annotation { "Feature Type Name" : "Feature", "Feature Type Description" : "" }
export const myFeature = defineFeature(function(context is Context, id is Id, definition is map)
    precondition{}
    {
        {
            var Q0;
            Q0=qCreatedBy(makeId("Front.planeOp"),FACE);
            var sketch = newSketch(context, id + "F0", { "sketchPlane" : qUnion([Q0])});
            skLineSegment(sketch, "E0", {"start": v(0, 0) * mm, "end": v(42.86, 0) * mm});
            skLineSegment(sketch, "E1", {"start": v(42.86, 0) * mm, "end": v(42.86, 3.17) * mm});
            skLineSegment(sketch, "E2", {"start": v(42.86, 3.17) * mm, "end": v(45.24, 3.17) * mm});
            skLineSegment(sketch, "E3", {"start": v(45.24, 3.17) * mm, "end": v(45.24, 0) * mm});
            skLineSegment(sketch, "E4", {"start": v(45.24, 0) * mm, "end": v(153.99, 0) * mm});
            skLineSegment(sketch, "E5", {"start": v(153.99, 0) * mm, "end": v(153.99, 3.17) * mm});
            skLineSegment(sketch, "E6", {"start": v(153.99, 3.17) * mm, "end": v(156.37, 3.17) * mm});
            skLineSegment(sketch, "E7", {"start": v(156.37, 3.17) * mm, "end": v(156.37, 0) * mm});
            skLineSegment(sketch, "E8", {"start": v(156.37, 0) * mm, "end": v(177.8, 0) * mm});
            skLineSegment(sketch, "E9.0", {"start": v(162.72, 5.08) * mm, "end": v(177.8, 5.08) * mm});
            skLineSegment(sketch, "E9.1", {"start": v(161.45, 6.98) * mm, "end": v(161.45, 6.35) * mm});
            skLineSegment(sketch, "E9.2", {"start": v(150.18, 8.25) * mm, "end": v(160.18, 8.25) * mm});
            skLineSegment(sketch, "E9.3", {"start": v(148.9, 6.35) * mm, "end": v(148.9, 6.98) * mm});
            skLineSegment(sketch, "E9.4", {"start": v(51.6, 5.08) * mm, "end": v(147.64, 5.08) * mm});
            skLineSegment(sketch, "E9.5", {"start": v(0, 5.08) * mm, "end": v(36.51, 5.08) * mm});
            skLineSegment(sketch, "E9.6", {"start": v(37.78, 6.35) * mm, "end": v(37.78, 6.98) * mm});
            skLineSegment(sketch, "E9.7", {"start": v(39.05, 8.25) * mm, "end": v(49.05, 8.25) * mm});
            skLineSegment(sketch, "E9.8", {"start": v(50.32, 6.98) * mm, "end": v(50.32, 6.35) * mm});
            skLineSegment(sketch, "E10", {"start": v(0, 0) * mm, "end": v(0, 5.08) * mm});
            skLineSegment(sketch, "E11", {"start": v(177.8, 0) * mm, "end": v(177.8, 5.08) * mm});
            skPoint(sketch, "E12.visualSharp", {"position": v(161.45, 5.08) * mm});
            skArc(sketch, "E12.filletArc", {"start": v(161.45, 6.35) * mm, "mid": v(161.82, 5.45) * mm, "end": v(162.72, 5.08) * mm});
            skPoint(sketch, "E13.visualSharp", {"position": v(161.45, 8.25) * mm});
            skArc(sketch, "E13.filletArc", {"start": v(161.45, 6.98) * mm, "mid": v(161.08, 7.88) * mm, "end": v(160.18, 8.25) * mm});
            skPoint(sketch, "E14.visualSharp", {"position": v(148.9, 8.25) * mm});
            skArc(sketch, "E14.filletArc", {"start": v(150.18, 8.25) * mm, "mid": v(149.28, 7.88) * mm, "end": v(148.9, 6.98) * mm});
            skPoint(sketch, "E15.visualSharp", {"position": v(148.9, 5.08) * mm});
            skArc(sketch, "E15.filletArc", {"start": v(147.64, 5.08) * mm, "mid": v(148.54, 5.45) * mm, "end": v(148.9, 6.35) * mm});
            skPoint(sketch, "E16.visualSharp", {"position": v(50.32, 5.08) * mm});
            skArc(sketch, "E16.filletArc", {"start": v(50.32, 6.35) * mm, "mid": v(50.7, 5.45) * mm, "end": v(51.6, 5.08) * mm});
            skPoint(sketch, "E17.visualSharp", {"position": v(50.32, 8.25) * mm});
            skArc(sketch, "E17.filletArc", {"start": v(50.32, 6.98) * mm, "mid": v(49.95, 7.88) * mm, "end": v(49.05, 8.25) * mm});
            skPoint(sketch, "E18.visualSharp", {"position": v(37.78, 8.25) * mm});
            skArc(sketch, "E18.filletArc", {"start": v(39.05, 8.25) * mm, "mid": v(38.15, 7.88) * mm, "end": v(37.78, 6.98) * mm});
            skPoint(sketch, "E19.visualSharp", {"position": v(37.78, 5.08) * mm});
            skArc(sketch, "E19.filletArc", {"start": v(36.51, 5.08) * mm, "mid": v(37.41, 5.45) * mm, "end": v(37.78, 6.35) * mm});
            skSolve(sketch);
        }
        {
            var Q0;
            Q0 = qSketchRegion(id + "F0", true);
            extrude(context, id + "F1", {"entities" : qUnion([Q0]), "endBound" : BoundingType.SYMMETRIC, "depth" : 44.45 * mm, "offsetDistance" : 25.4 * mm});
        }
        {
            var Q0;
            Q0=qCreatedBy(makeId("Top.planeOp"),FACE);
            var sketch = newSketch(context, id + "F2", { "sketchPlane" : qUnion([Q0])});
            skLineSegment(sketch, "E20", {"start": v(-14.1, 0) * mm, "end": v(126.69, 0) * mm, "construction": true});
            skLineSegment(sketch, "E21.bottom", {"start": v(27.6, 17.15) * mm, "end": v(29.65, 17.15) * mm});
            skLineSegment(sketch, "E21.top", {"start": v(16.56, 2.54) * mm, "end": v(29.65, 2.54) * mm});
            skLineSegment(sketch, "E21.left", {"start": v(5.08, 15.37) * mm, "end": v(5.08, 6.83) * mm});
            skLineSegment(sketch, "E21.right", {"start": v(31.43, 15.37) * mm, "end": v(31.43, 4.32) * mm});
            skLineSegment(sketch, "E22.bottom", {"start": v(64.83, 17.14) * mm, "end": v(66.99, 17.14) * mm});
            skLineSegment(sketch, "E22.top", {"start": v(68.15, 2.54) * mm, "end": v(70.3, 2.54) * mm});
            skLineSegment(sketch, "E22.left", {"start": v(56.67, 8.99) * mm, "end": v(56.67, 6.83) * mm});
            skLineSegment(sketch, "E23", {"start": v(8.12, 5.58) * mm, "end": v(16.65, 14.1) * mm});
            skLineSegment(sketch, "E24", {"start": v(15.3, 5.58) * mm, "end": v(26.35, 16.62) * mm});
            skArc(sketch, "E25.filletArc", {"start": v(27.6, 17.15) * mm, "mid": v(26.93, 17) * mm, "end": v(26.35, 16.62) * mm});
            skPoint(sketch, "E26.visualSharp", {"position": v(31.43, 17.14) * mm});
            skArc(sketch, "E26.filletArc", {"start": v(31.43, 15.37) * mm, "mid": v(30.91, 16.62) * mm, "end": v(29.65, 17.15) * mm});
            skPoint(sketch, "E27.visualSharp", {"position": v(31.43, 2.54) * mm});
            skArc(sketch, "E27.filletArc", {"start": v(29.65, 2.54) * mm, "mid": v(30.91, 3.06) * mm, "end": v(31.43, 4.32) * mm});
            skArc(sketch, "E28.filletArc", {"start": v(15.3, 5.58) * mm, "mid": v(14.91, 3.64) * mm, "end": v(16.56, 2.54) * mm});
            skPoint(sketch, "E29.visualSharp", {"position": v(5.08, 2.54) * mm});
            skArc(sketch, "E29.filletArc", {"start": v(5.08, 6.83) * mm, "mid": v(6.18, 5.19) * mm, "end": v(8.12, 5.58) * mm});
            skLineSegment(sketch, "E30", {"start": v(15.4, 17.14) * mm, "end": v(6.86, 17.14) * mm});
            skPoint(sketch, "E31.visualSharp", {"position": v(19.69, 17.14) * mm});
            skArc(sketch, "E31.filletArc", {"start": v(16.65, 14.1) * mm, "mid": v(17.04, 16.05) * mm, "end": v(15.4, 17.15) * mm});
            skPoint(sketch, "E32.visualSharp", {"position": v(5.08, 17.14) * mm});
            skArc(sketch, "E32.filletArc", {"start": v(6.86, 17.14) * mm, "mid": v(5.6, 16.62) * mm, "end": v(5.08, 15.37) * mm});
            skLineSegment(sketch, "E33", {"start": v(59.7, 5.58) * mm, "end": v(68.24, 14.1) * mm});
            skLineSegment(sketch, "E34", {"start": v(66.9, 5.58) * mm, "end": v(77.94, 16.62) * mm});
            skLineSegment(sketch, "E35", {"start": v(71.56, 3.06) * mm, "end": v(82.61, 14.1) * mm});
            skLineSegment(sketch, "E36", {"start": v(81.26, 5.58) * mm, "end": v(92.31, 16.62) * mm});
            skLineSegment(sketch, "E37", {"start": v(85.93, 3.06) * mm, "end": v(96.98, 14.1) * mm});
            skLineSegment(sketch, "E38", {"start": v(95.63, 5.58) * mm, "end": v(106.68, 16.62) * mm});
            skLineSegment(sketch, "E39", {"start": v(100.3, 3.06) * mm, "end": v(111.35, 14.1) * mm});
            skLineSegment(sketch, "E40", {"start": v(110, 5.58) * mm, "end": v(121.05, 16.62) * mm});
            skLineSegment(sketch, "E41", {"start": v(114.67, 3.06) * mm, "end": v(125.72, 14.1) * mm});
            skLineSegment(sketch, "E42", {"start": v(124.37, 5.58) * mm, "end": v(135.42, 16.62) * mm});
            skLineSegment(sketch, "E43", {"start": v(129.04, 3.06) * mm, "end": v(140.09, 14.1) * mm});
            skLineSegment(sketch, "E44", {"start": v(136.6, 3.45) * mm, "end": v(141.65, 8.49) * mm});
            skLineSegment(sketch, "E45.trimOffspring", {"start": v(79.2, 17.15) * mm, "end": v(81.35, 17.15) * mm});
            skLineSegment(sketch, "E46.trimOffspring", {"start": v(82.52, 2.54) * mm, "end": v(84.67, 2.54) * mm});
            skLineSegment(sketch, "E47.trimOffspring", {"start": v(93.57, 17.15) * mm, "end": v(95.72, 17.15) * mm});
            skLineSegment(sketch, "E48.trimOffspring", {"start": v(107.94, 17.15) * mm, "end": v(110.1, 17.15) * mm});
            skLineSegment(sketch, "E49.trimOffspring", {"start": v(96.89, 2.54) * mm, "end": v(99.04, 2.54) * mm});
            skLineSegment(sketch, "E50.trimOffspring", {"start": v(122.3, 17.15) * mm, "end": v(124.46, 17.15) * mm});
            skLineSegment(sketch, "E51.trimOffspring", {"start": v(111.26, 2.54) * mm, "end": v(113.41, 2.54) * mm});
            skLineSegment(sketch, "E52.trimOffspring", {"start": v(136.67, 17.15) * mm, "end": v(138.83, 17.15) * mm});
            skLineSegment(sketch, "E53.trimOffspring", {"start": v(125.62, 2.54) * mm, "end": v(127.78, 2.54) * mm});
            skLineSegment(sketch, "E54.trimOffspring", {"start": v(136.98, 2.54) * mm, "end": v(140.78, 2.54) * mm});
            skLineSegment(sketch, "E55.trimOffspring", {"start": v(142.56, 8.11) * mm, "end": v(142.56, 4.32) * mm});
            skPoint(sketch, "E56.visualSharp", {"position": v(71.28, 17.14) * mm});
            skArc(sketch, "E56.filletArc", {"start": v(68.24, 14.1) * mm, "mid": v(68.63, 16.05) * mm, "end": v(66.99, 17.14) * mm});
            skPoint(sketch, "E57.visualSharp", {"position": v(56.67, 2.54) * mm});
            skArc(sketch, "E57.filletArc", {"start": v(56.67, 6.83) * mm, "mid": v(57.77, 5.19) * mm, "end": v(59.7, 5.58) * mm});
            skPoint(sketch, "E58.visualSharp", {"position": v(56.67, 17.14) * mm});
            skPoint(sketch, "E59.visualSharp", {"position": v(63.86, 2.54) * mm});
            skArc(sketch, "E59.filletArc", {"start": v(66.9, 5.58) * mm, "mid": v(66.5, 3.64) * mm, "end": v(68.15, 2.54) * mm});
            skPoint(sketch, "E60.visualSharp", {"position": v(71.04, 2.54) * mm});
            skArc(sketch, "E60.filletArc", {"start": v(70.3, 2.54) * mm, "mid": v(70.99, 2.68) * mm, "end": v(71.56, 3.06) * mm});
            skPoint(sketch, "E61.visualSharp", {"position": v(85.65, 17.14) * mm});
            skArc(sketch, "E61.filletArc", {"start": v(82.61, 14.1) * mm, "mid": v(83, 16.05) * mm, "end": v(81.35, 17.14) * mm});
            skPoint(sketch, "E62.visualSharp", {"position": v(78.46, 17.14) * mm});
            skArc(sketch, "E62.filletArc", {"start": v(79.2, 17.15) * mm, "mid": v(78.52, 17) * mm, "end": v(77.94, 16.62) * mm});
            skPoint(sketch, "E63.visualSharp", {"position": v(92.83, 17.14) * mm});
            skArc(sketch, "E63.filletArc", {"start": v(93.57, 17.14) * mm, "mid": v(92.89, 17) * mm, "end": v(92.31, 16.62) * mm});
            skPoint(sketch, "E64.visualSharp", {"position": v(100.02, 17.14) * mm});
            skArc(sketch, "E64.filletArc", {"start": v(96.98, 14.1) * mm, "mid": v(97.37, 16.05) * mm, "end": v(95.72, 17.15) * mm});
            skPoint(sketch, "E65.visualSharp", {"position": v(85.41, 2.54) * mm});
            skArc(sketch, "E65.filletArc", {"start": v(84.67, 2.54) * mm, "mid": v(85.35, 2.68) * mm, "end": v(85.93, 3.06) * mm});
            skPoint(sketch, "E66.visualSharp", {"position": v(78.23, 2.54) * mm});
            skArc(sketch, "E66.filletArc", {"start": v(81.26, 5.58) * mm, "mid": v(80.88, 3.64) * mm, "end": v(82.52, 2.54) * mm});
            skPoint(sketch, "E67.visualSharp", {"position": v(107.2, 17.14) * mm});
            skArc(sketch, "E67.filletArc", {"start": v(107.94, 17.15) * mm, "mid": v(107.26, 17) * mm, "end": v(106.68, 16.62) * mm});
            skPoint(sketch, "E68.visualSharp", {"position": v(114.38, 17.14) * mm});
            skArc(sketch, "E68.filletArc", {"start": v(111.35, 14.1) * mm, "mid": v(111.73, 16.05) * mm, "end": v(110.1, 17.15) * mm});
            skPoint(sketch, "E69.visualSharp", {"position": v(99.78, 2.54) * mm});
            skArc(sketch, "E69.filletArc", {"start": v(99.04, 2.54) * mm, "mid": v(99.72, 2.68) * mm, "end": v(100.3, 3.06) * mm});
            skPoint(sketch, "E70.visualSharp", {"position": v(92.6, 2.54) * mm});
            skArc(sketch, "E70.filletArc", {"start": v(95.63, 5.58) * mm, "mid": v(95.24, 3.64) * mm, "end": v(96.89, 2.54) * mm});
            skPoint(sketch, "E71.visualSharp", {"position": v(106.96, 2.54) * mm});
            skArc(sketch, "E71.filletArc", {"start": v(110, 5.58) * mm, "mid": v(109.61, 3.64) * mm, "end": v(111.26, 2.54) * mm});
            skPoint(sketch, "E72.visualSharp", {"position": v(114.15, 2.54) * mm});
            skArc(sketch, "E72.filletArc", {"start": v(113.41, 2.54) * mm, "mid": v(114.1, 2.68) * mm, "end": v(114.67, 3.06) * mm});
            skPoint(sketch, "E73.visualSharp", {"position": v(128.75, 17.14) * mm});
            skArc(sketch, "E73.filletArc", {"start": v(125.72, 14.1) * mm, "mid": v(126.1, 16.05) * mm, "end": v(124.46, 17.15) * mm});
            skPoint(sketch, "E74.visualSharp", {"position": v(121.57, 17.14) * mm});
            skArc(sketch, "E74.filletArc", {"start": v(122.3, 17.15) * mm, "mid": v(121.62, 17) * mm, "end": v(121.05, 16.62) * mm});
            skPoint(sketch, "E75.visualSharp", {"position": v(135.94, 17.14) * mm});
            skArc(sketch, "E75.filletArc", {"start": v(136.67, 17.14) * mm, "mid": v(136, 17) * mm, "end": v(135.42, 16.62) * mm});
            skPoint(sketch, "E76.visualSharp", {"position": v(128.52, 2.54) * mm});
            skArc(sketch, "E76.filletArc", {"start": v(127.78, 2.54) * mm, "mid": v(128.46, 2.68) * mm, "end": v(129.04, 3.06) * mm});
            skPoint(sketch, "E77.visualSharp", {"position": v(121.33, 2.54) * mm});
            skArc(sketch, "E77.filletArc", {"start": v(124.37, 5.58) * mm, "mid": v(123.98, 3.64) * mm, "end": v(125.62, 2.54) * mm});
            skPoint(sketch, "E78.visualSharp", {"position": v(142.56, 2.54) * mm});
            skArc(sketch, "E78.filletArc", {"start": v(140.78, 2.54) * mm, "mid": v(142.04, 3.06) * mm, "end": v(142.56, 4.32) * mm});
            skPoint(sketch, "E79.visualSharp", {"position": v(135.7, 2.54) * mm});
            skArc(sketch, "E79.filletArc", {"start": v(136.6, 3.45) * mm, "mid": v(136.5, 2.87) * mm, "end": v(136.98, 2.54) * mm});
            skPoint(sketch, "E80.visualSharp", {"position": v(142.56, 9.4) * mm});
            skArc(sketch, "E80.filletArc", {"start": v(142.56, 8.11) * mm, "mid": v(142.23, 8.6) * mm, "end": v(141.65, 8.49) * mm});
            skArc(sketch, "E81.MirrorCS", {"start": v(143.12, -17.14) * mm, "mid": v(142.85, -17.26) * mm, "end": v(142.56, -17.32) * mm});
            skArc(sketch, "E82.MirrorCS", {"start": v(136.6, -3.45) * mm, "mid": v(136.5, -2.87) * mm, "end": v(136.98, -2.54) * mm});
            skArc(sketch, "E83.MirrorCS", {"start": v(107.94, -17.15) * mm, "mid": v(107.26, -17) * mm, "end": v(106.68, -16.62) * mm});
            skArc(sketch, "E84.MirrorCS", {"start": v(93.57, -17.14) * mm, "mid": v(92.89, -17) * mm, "end": v(92.31, -16.62) * mm});
            skArc(sketch, "E85.MirrorCS", {"start": v(99.04, -2.54) * mm, "mid": v(99.72, -2.68) * mm, "end": v(100.3, -3.06) * mm});
            skArc(sketch, "E86.MirrorCS", {"start": v(122.3, -17.15) * mm, "mid": v(121.62, -17) * mm, "end": v(121.05, -16.62) * mm});
            skArc(sketch, "E87.MirrorCS", {"start": v(84.67, -2.54) * mm, "mid": v(85.35, -2.68) * mm, "end": v(85.93, -3.06) * mm});
            skArc(sketch, "E88.MirrorCS", {"start": v(136.67, -17.14) * mm, "mid": v(136, -17) * mm, "end": v(135.42, -16.62) * mm});
            skArc(sketch, "E89.MirrorCS", {"start": v(142.56, -8.11) * mm, "mid": v(142.23, -8.6) * mm, "end": v(141.65, -8.49) * mm});
            skArc(sketch, "E90.MirrorCS", {"start": v(113.41, -2.54) * mm, "mid": v(114.1, -2.68) * mm, "end": v(114.67, -3.06) * mm});
            skLineSegment(sketch, "E91.MirrorCS", {"start": v(142.56, -8.11) * mm, "end": v(142.56, -4.32) * mm});
            skLineSegment(sketch, "E92.MirrorCS", {"start": v(136.98, -2.54) * mm, "end": v(140.78, -2.54) * mm});
            skArc(sketch, "E93.MirrorCS", {"start": v(127.78, -2.54) * mm, "mid": v(128.46, -2.68) * mm, "end": v(129.04, -3.06) * mm});
            skArc(sketch, "E94.MirrorCS", {"start": v(79.2, -17.15) * mm, "mid": v(78.52, -17) * mm, "end": v(77.94, -16.62) * mm});
            skArc(sketch, "E95.MirrorCS", {"start": v(70.3, -2.54) * mm, "mid": v(70.99, -2.68) * mm, "end": v(71.56, -3.06) * mm});
            skLineSegment(sketch, "E96.MirrorCS", {"start": v(142.56, -17.32) * mm, "end": v(142.56, -15.37) * mm});
            skLineSegment(sketch, "E97.MirrorCS", {"start": v(68.15, -2.54) * mm, "end": v(70.3, -2.54) * mm});
            skLineSegment(sketch, "E98.MirrorCS", {"start": v(136.6, -3.45) * mm, "end": v(141.65, -8.49) * mm});
            skLineSegment(sketch, "E99.MirrorCS", {"start": v(111.26, -2.54) * mm, "end": v(113.41, -2.54) * mm});
            skLineSegment(sketch, "E100.MirrorCS", {"start": v(136.67, -17.15) * mm, "end": v(143.32, -17.15) * mm});
            skLineSegment(sketch, "E101.MirrorCS", {"start": v(122.3, -17.15) * mm, "end": v(124.46, -17.15) * mm});
            skLineSegment(sketch, "E102.MirrorCS", {"start": v(79.2, -17.15) * mm, "end": v(81.35, -17.15) * mm});
            skLineSegment(sketch, "E103.MirrorCS", {"start": v(82.52, -2.54) * mm, "end": v(84.67, -2.54) * mm});
            skLineSegment(sketch, "E104.MirrorCS", {"start": v(96.89, -2.54) * mm, "end": v(99.04, -2.54) * mm});
            skLineSegment(sketch, "E105.MirrorCS", {"start": v(93.57, -17.15) * mm, "end": v(95.72, -17.15) * mm});
            skArc(sketch, "E106.MirrorCS", {"start": v(140.78, -2.54) * mm, "mid": v(142.04, -3.06) * mm, "end": v(142.56, -4.32) * mm});
            skLineSegment(sketch, "E107.MirrorCS", {"start": v(107.94, -17.15) * mm, "end": v(110.1, -17.15) * mm});
            skLineSegment(sketch, "E108.MirrorCS", {"start": v(125.62, -2.54) * mm, "end": v(127.78, -2.54) * mm});
            skLineSegment(sketch, "E109.MirrorCS", {"start": v(27.6, -17.15) * mm, "end": v(29.65, -17.15) * mm});
            skArc(sketch, "E110.MirrorCS", {"start": v(27.6, -17.15) * mm, "mid": v(26.93, -17) * mm, "end": v(26.35, -16.62) * mm});
            skArc(sketch, "E111.MirrorCS", {"start": v(6.86, -17.14) * mm, "mid": v(5.6, -16.62) * mm, "end": v(5.08, -15.37) * mm});
            skArc(sketch, "E112.MirrorCS", {"start": v(95.63, -5.58) * mm, "mid": v(95.24, -3.64) * mm, "end": v(96.89, -2.54) * mm});
            skPoint(sketch, "E113.MirrorP", {"position": v(142.56, -2.54) * mm});
            skArc(sketch, "E114.MirrorCS", {"start": v(29.65, -2.54) * mm, "mid": v(30.91, -3.06) * mm, "end": v(31.43, -4.32) * mm});
            skArc(sketch, "E115.MirrorCS", {"start": v(111.35, -14.1) * mm, "mid": v(111.73, -16.05) * mm, "end": v(110.1, -17.15) * mm});
            skArc(sketch, "E116.MirrorCS", {"start": v(124.37, -5.58) * mm, "mid": v(123.98, -3.64) * mm, "end": v(125.62, -2.54) * mm});
            skArc(sketch, "E117.MirrorCS", {"start": v(82.61, -14.1) * mm, "mid": v(83, -16.05) * mm, "end": v(81.35, -17.14) * mm});
            skArc(sketch, "E118.MirrorCS", {"start": v(66.9, -5.58) * mm, "mid": v(66.5, -3.64) * mm, "end": v(68.15, -2.54) * mm});
            skArc(sketch, "E119.MirrorCS", {"start": v(81.26, -5.58) * mm, "mid": v(80.88, -3.64) * mm, "end": v(82.52, -2.54) * mm});
            skLineSegment(sketch, "E120.MirrorCS", {"start": v(15.4, -17.14) * mm, "end": v(6.86, -17.14) * mm});
            skArc(sketch, "E121.MirrorCS", {"start": v(142.56, -15.37) * mm, "mid": v(143.2, -16.14) * mm, "end": v(143.32, -17.15) * mm});
            skPoint(sketch, "E122.MirrorP", {"position": v(142.56, -16.58) * mm});
            skArc(sketch, "E123.MirrorCS", {"start": v(125.72, -14.1) * mm, "mid": v(126.1, -16.05) * mm, "end": v(124.46, -17.15) * mm});
            skArc(sketch, "E124.MirrorCS", {"start": v(96.98, -14.1) * mm, "mid": v(97.37, -16.05) * mm, "end": v(95.72, -17.15) * mm});
            skPoint(sketch, "E125.MirrorP", {"position": v(135.7, -2.54) * mm});
            skArc(sketch, "E126.MirrorCS", {"start": v(16.65, -14.1) * mm, "mid": v(17.04, -16.05) * mm, "end": v(15.4, -17.15) * mm});
            skArc(sketch, "E127.MirrorCS", {"start": v(5.08, -6.83) * mm, "mid": v(6.18, -5.19) * mm, "end": v(8.12, -5.58) * mm});
            skArc(sketch, "E128.MirrorCS", {"start": v(110, -5.58) * mm, "mid": v(109.61, -3.64) * mm, "end": v(111.26, -2.54) * mm});
            skArc(sketch, "E129.MirrorCS", {"start": v(15.3, -5.58) * mm, "mid": v(14.91, -3.64) * mm, "end": v(16.56, -2.54) * mm});
            skArc(sketch, "E130.MirrorCS", {"start": v(31.43, -15.37) * mm, "mid": v(30.91, -16.62) * mm, "end": v(29.65, -17.15) * mm});
            skLineSegment(sketch, "E131.MirrorCS", {"start": v(110, -5.58) * mm, "end": v(121.05, -16.62) * mm});
            skLineSegment(sketch, "E132.MirrorCS", {"start": v(95.63, -5.58) * mm, "end": v(106.68, -16.62) * mm});
            skPoint(sketch, "E133.MirrorP", {"position": v(99.78, -2.54) * mm});
            skLineSegment(sketch, "E134.MirrorCS", {"start": v(71.56, -3.06) * mm, "end": v(82.61, -14.1) * mm});
            skLineSegment(sketch, "E135.MirrorCS", {"start": v(31.43, -15.37) * mm, "end": v(31.43, -4.32) * mm});
            skPoint(sketch, "E136.MirrorP", {"position": v(114.38, -17.14) * mm});
            skPoint(sketch, "E137.MirrorP", {"position": v(19.69, -17.14) * mm});
            skPoint(sketch, "E138.MirrorP", {"position": v(142.56, -17.14) * mm});
            skLineSegment(sketch, "E139.MirrorCS", {"start": v(81.26, -5.58) * mm, "end": v(92.31, -16.62) * mm});
            skPoint(sketch, "E140.MirrorP", {"position": v(31.43, -2.54) * mm});
            skPoint(sketch, "E141.MirrorP", {"position": v(100.02, -17.14) * mm});
            skPoint(sketch, "E142.MirrorP", {"position": v(114.15, -2.54) * mm});
            skPoint(sketch, "E143.MirrorP", {"position": v(5.08, -17.14) * mm});
            skLineSegment(sketch, "E144.MirrorCS", {"start": v(114.67, -3.06) * mm, "end": v(125.72, -14.1) * mm});
            skPoint(sketch, "E145.MirrorP", {"position": v(92.83, -17.14) * mm});
            skPoint(sketch, "E146.MirrorP", {"position": v(106.96, -2.54) * mm});
            skPoint(sketch, "E147.MirrorP", {"position": v(85.41, -2.54) * mm});
            skLineSegment(sketch, "E148.MirrorCS", {"start": v(129.04, -3.06) * mm, "end": v(143.12, -17.14) * mm});
            skLineSegment(sketch, "E149.MirrorCS", {"start": v(66.9, -5.58) * mm, "end": v(77.94, -16.62) * mm});
            skPoint(sketch, "E150.MirrorP", {"position": v(142.56, -9.4) * mm});
            skPoint(sketch, "E151.MirrorP", {"position": v(78.23, -2.54) * mm});
            skPoint(sketch, "E152.MirrorP", {"position": v(121.57, -17.14) * mm});
            skPoint(sketch, "E153.MirrorP", {"position": v(121.33, -2.54) * mm});
            skPoint(sketch, "E154.MirrorP", {"position": v(31.43, -17.14) * mm});
            skPoint(sketch, "E155.MirrorP", {"position": v(92.6, -2.54) * mm});
            skPoint(sketch, "E156.MirrorP", {"position": v(85.65, -17.14) * mm});
            skPoint(sketch, "E157.MirrorP", {"position": v(5.08, -2.54) * mm});
            skLineSegment(sketch, "E158.MirrorCS", {"start": v(100.3, -3.06) * mm, "end": v(111.35, -14.1) * mm});
            skLineSegment(sketch, "E159.MirrorCS", {"start": v(85.93, -3.06) * mm, "end": v(96.98, -14.1) * mm});
            skPoint(sketch, "E160.MirrorP", {"position": v(128.52, -2.54) * mm});
            skPoint(sketch, "E161.MirrorP", {"position": v(107.2, -17.14) * mm});
            skPoint(sketch, "E162.MirrorP", {"position": v(128.75, -17.14) * mm});
            skPoint(sketch, "E163.MirrorP", {"position": v(78.46, -17.14) * mm});
            skLineSegment(sketch, "E164.MirrorCS", {"start": v(16.56, -2.54) * mm, "end": v(29.65, -2.54) * mm});
            skLineSegment(sketch, "E165.MirrorCS", {"start": v(8.12, -5.58) * mm, "end": v(16.65, -14.1) * mm});
            skLineSegment(sketch, "E166.MirrorCS", {"start": v(5.08, -15.37) * mm, "end": v(5.08, -6.83) * mm});
            skLineSegment(sketch, "E167.MirrorCS", {"start": v(15.3, -5.58) * mm, "end": v(26.35, -16.62) * mm});
            skLineSegment(sketch, "E168.MirrorCS", {"start": v(124.37, -5.58) * mm, "end": v(135.42, -16.62) * mm});
            skPoint(sketch, "E169.MirrorP", {"position": v(135.94, -17.14) * mm});
            skPoint(sketch, "E170.startSnap0", {"position": v(63.98, 9.84) * mm});
            skLineSegment(sketch, "E171", {"start": v(57.2, 10.24) * mm, "end": v(63.57, 16.62) * mm});
            skPoint(sketch, "E58.filletArc.start.orphan", {"position": v(59.72, 17.14) * mm});
            skPoint(sketch, "E172.orphan", {"position": v(56.67, 15.37) * mm});
            skPoint(sketch, "E173.visualSharp", {"position": v(56.67, 9.72) * mm});
            skArc(sketch, "E173.filletArc", {"start": v(57.2, 10.24) * mm, "mid": v(56.8, 9.67) * mm, "end": v(56.67, 8.99) * mm});
            skPoint(sketch, "E174.visualSharp", {"position": v(64.1, 17.14) * mm});
            skArc(sketch, "E174.filletArc", {"start": v(64.83, 17.14) * mm, "mid": v(64.15, 17) * mm, "end": v(63.57, 16.62) * mm});
            skArc(sketch, "E175.MirrorCS", {"start": v(57.2, -10.24) * mm, "mid": v(56.8, -9.67) * mm, "end": v(56.67, -8.99) * mm});
            skArc(sketch, "E176.MirrorCS", {"start": v(64.83, -17.14) * mm, "mid": v(64.15, -17) * mm, "end": v(63.57, -16.62) * mm});
            skLineSegment(sketch, "E177.MirrorCS", {"start": v(56.67, -8.99) * mm, "end": v(56.67, -6.83) * mm});
            skArc(sketch, "E178.MirrorCS", {"start": v(68.24, -14.1) * mm, "mid": v(68.63, -16.05) * mm, "end": v(66.99, -17.14) * mm});
            skArc(sketch, "E179.MirrorCS", {"start": v(56.67, -6.83) * mm, "mid": v(57.77, -5.19) * mm, "end": v(59.7, -5.58) * mm});
            skLineSegment(sketch, "E180.MirrorCS", {"start": v(57.2, -10.24) * mm, "end": v(63.57, -16.62) * mm});
            skLineSegment(sketch, "E181.MirrorCS", {"start": v(64.83, -17.14) * mm, "end": v(66.99, -17.14) * mm});
            skLineSegment(sketch, "E182.MirrorCS", {"start": v(59.7, -5.58) * mm, "end": v(68.24, -14.1) * mm});
            skPoint(sketch, "E183.MirrorP", {"position": v(63.98, -9.84) * mm});
            skPoint(sketch, "E184.MirrorP", {"position": v(59.72, -17.14) * mm});
            skPoint(sketch, "E185.MirrorP", {"position": v(56.67, -15.37) * mm});
            skPoint(sketch, "E186.MirrorP", {"position": v(56.67, -9.72) * mm});
            skPoint(sketch, "E187.MirrorP", {"position": v(56.67, -17.14) * mm});
            skPoint(sketch, "E188.MirrorP", {"position": v(64.1, -17.14) * mm});
            skPoint(sketch, "E189.newPointA", {"position": v(143.32, 17.15) * mm});
            skPoint(sketch, "E189.newPointB", {"position": v(143.12, 17.14) * mm});
            skArc(sketch, "E189.filletArc", {"start": v(140.09, 14.1) * mm, "mid": v(140.47, 16.05) * mm, "end": v(138.83, 17.14) * mm});
            skSolve(sketch);
        }
        {
            var Q0;
            Q0 = qSketchRegion(id + "F2", true);
            extrude(context, id + "F3", {"entities" : qUnion([Q0]), "operationType" : NewBodyOperationType.REMOVE, "endBound" : BoundingType.THROUGH_ALL, "depth" : 25.4 * mm, "offsetDistance" : 25.4 * mm});
        }
        {
            var Q0;
            Q0=qCreatedBy(makeId("Top.planeOp"),FACE);
            var sketch = newSketch(context, id + "F4", { "sketchPlane" : qUnion([Q0])});
            skText(sketch, "E190", { "text": "72", "fontName": "RobotoSlab-Bold.ttf"});
            skLineSegment(sketch, "E191", {"start": v(-40.93, 0) * mm, "end": v(181.72, 0) * mm, "construction": true});
            const initialGuessF4  = {"E190": [0.00701, 0.01567, 0, -1, 0.02022]};
            skSetInitialGuess(sketch, initialGuessF4);
            skSolve(sketch);
        }
        {
            var Q0;
            Q0 = qSketchRegion(id + "F4", true);
            extrude(context, id + "F5", {"entities" : qUnion([Q0]), "operationType" : NewBodyOperationType.ADD, "depth" : 25.4 * mm, "offsetDistance" : 25.4 * mm});
        }
        {
            var Q0;
            Q0=qCreatedBy(makeId("Top.planeOp"),FACE);
            var sketch = newSketch(context, id + "F6", { "sketchPlane" : qUnion([Q0])});
            skLineSegment(sketch, "E192", {"start": v(-21.34, 0) * mm, "end": v(221.51, 0) * mm, "construction": true});
            skText(sketch, "E193", { "text": "Badger Patrol", "fontName": "OpenSans-Bold.ttf"});
            skText(sketch, "E194", { "text": "Badger Patrol", "fontName": "OpenSans-Bold.ttf"});
            const initialGuessF6  = {"E193": [0.0546, -0.01841, 1, 0, 0.00952], "E194": [0.1447, 0.01841, -1, 0, 0.00952]};
            skSetInitialGuess(sketch, initialGuessF6);
            skSolve(sketch);
        }
        {
            var Q0;
            Q0 = qSketchRegion(id + "F6", true);
            extrude(context, id + "F7", {"entities" : qUnion([Q0]), "operationType" : NewBodyOperationType.ADD, "depth" : 25.4 * mm, "offsetDistance" : 25.4 * mm});
        }
        {
            var Q0;
            Q0=qCreatedBy(makeId("Front.planeOp"),FACE);
            var sketch = newSketch(context, id + "F8", { "sketchPlane" : qUnion([Q0])});
            skLineSegment(sketch, "E195", {"start": v(-8.89, 5.08) * mm, "end": v(186.85, 5.08) * mm, "construction": true});
            skLineSegment(sketch, "E196", {"start": v(0, 29.6) * mm, "end": v(0, -25.47) * mm, "construction": true});
            skLineSegment(sketch, "E197", {"start": v(177.8, 29.6) * mm, "end": v(177.8, -28.87) * mm, "construction": true});
            skPoint(sketch, "E198", {"position": v(0, 5.08) * mm});
            skPoint(sketch, "E199", {"position": v(177.8, 5.08) * mm});
            skPoint(sketch, "E200", {"position": v(147.75, 14.48) * mm});
            skArc(sketch, "E201", {"start": v(188.97, 0.48) * mm, "mid": v(78.8, 21.35) * mm, "end": v(-29.32, -8.42) * mm});
            skLineSegment(sketch, "E202.bottom", {"start": v(-29.32, 61.14) * mm, "end": v(188.97, 61.14) * mm});
            skLineSegment(sketch, "E202.left", {"start": v(-29.32, 61.14) * mm, "end": v(-29.32, -8.42) * mm});
            skLineSegment(sketch, "E202.right", {"start": v(188.97, 61.14) * mm, "end": v(188.97, 0.48) * mm});
            skSolve(sketch);
        }
        {
            var Q0;
            Q0 = qSketchRegion(id + "F8", true);
            extrude(context, id + "F9", {"entities" : qUnion([Q0]), "operationType" : NewBodyOperationType.REMOVE, "endBound" : BoundingType.SYMMETRIC, "depth" : 76.2 * mm, "offsetDistance" : 25.4 * mm});
        }
        {
            var Q0;
            Q0=qCreatedBy(makeId("Front.planeOp"),FACE);
            var sketch = newSketch(context, id + "F10", { "sketchPlane" : qUnion([Q0])});
            skLineSegment(sketch, "E203", {"start": v(26.43, 13.34) * mm, "end": v(146.96, 13.34) * mm, "construction": true});
            skLineSegment(sketch, "E204", {"start": v(24.76, 3.18) * mm, "end": v(149.32, 3.18) * mm, "construction": true});
            skPoint(sketch, "E205", {"position": v(30.27, 13.34) * mm});
            skPoint(sketch, "E206", {"position": v(48.74, 3.18) * mm});
            skPoint(sketch, "E207", {"position": v(35.96, 7.3) * mm});
            skArc(sketch, "E208", {"start": v(30.27, 13.33) * mm, "mid": v(38.2, 5.88) * mm, "end": v(48.74, 3.18) * mm});
            skLineSegment(sketch, "E209", {"start": v(48.74, 3.18) * mm, "end": v(173.39, 3.18) * mm});
            skLineSegment(sketch, "E210", {"start": v(48.74, 25.04) * mm, "end": v(48.74, -6.06) * mm, "construction": true});
            skArc(sketch, "E211", {"start": v(32.57, 13.34) * mm, "mid": v(39.66, 7.26) * mm, "end": v(48.74, 5.08) * mm});
            skLineSegment(sketch, "E212", {"start": v(30.27, 13.34) * mm, "end": v(32.57, 13.34) * mm});
            skLineSegment(sketch, "E213", {"start": v(48.74, 5.08) * mm, "end": v(173.31, 5.08) * mm});
            skLineSegment(sketch, "E214", {"start": v(173.31, 5.08) * mm, "end": v(173.39, 3.18) * mm});
            skSolve(sketch);
        }
        {
            var Q0;
            Q0 = qSketchRegion(id + "F10", true);
            var Q1;
            Q1=sQuery(id+"F10.wireOp",EDGE,"E203");
            revolve(context, id + "F11", {"operationType" : NewBodyOperationType.ADD, "entities" : qUnion([Q0]), "axis" : qUnion([Q1]), "revolveType" : RevolveType.FULL});
        }
        {
            var Q0;
            Q0=qCreatedBy(makeId("Right.planeOp"),FACE);
            cPlane(context, id + "F12", {"entities" : qUnion([Q0]), "cplaneType" : CPlaneType.OFFSET, "offset" : 177.8 * mm, "width" : 152.4 * mm, "height" : 152.4 * mm});
        }
        {
            var Q0;
            Q0=qCreatedBy(makeId("Top.planeOp"),FACE);
            cPlane(context, id + "F13", {"entities" : qUnion([Q0]), "cplaneType" : CPlaneType.OFFSET, "offset" : 25.4 * mm, "width" : 152.4 * mm, "height" : 152.4 * mm});
        }
        {
            var Q0;
            Q0=qCreatedBy(id+"F13.planeOp",FACE);
            var sketch = newSketch(context, id + "F14", { "sketchPlane" : qUnion([Q0])});
            skLineSegment(sketch, "E215", {"start": v(-2.54, 0) * mm, "end": v(181.35, 0) * mm, "construction": true});
            skLineSegment(sketch, "E216", {"start": v(99.72, 60.45) * mm, "end": v(99.72, -50.12) * mm, "construction": true});
            skLineSegment(sketch, "E217", {"start": v(55.52, 31.77) * mm, "end": v(55.52, -34.92) * mm, "construction": true});
            skLineSegment(sketch, "E218", {"start": v(143.92, 33.14) * mm, "end": v(143.92, -35.72) * mm, "construction": true});
            skPoint(sketch, "E219", {"position": v(99.72, 39.37) * mm});
            skArc(sketch, "E220", {"start": v(76.17, 1.67) * mm, "mid": v(87.47, -3.36) * mm, "end": v(99.72, -5.08) * mm});
            skArc(sketch, "E221", {"start": v(77.1, 3.18) * mm, "mid": v(87.96, -1.65) * mm, "end": v(99.72, -3.3) * mm});
            skArc(sketch, "E222", {"start": v(79.4, -4.07) * mm, "mid": v(80.21, -4.44) * mm, "end": v(81.03, -4.8) * mm});
            skLineSegment(sketch, "E223", {"start": v(99.72, 39.37) * mm, "end": v(92.71, -10.49) * mm, "construction": true});
            skLineSegment(sketch, "E224", {"start": v(92.71, -10.49) * mm, "end": v(86.09, -8.18) * mm, "construction": true});
            skLineSegment(sketch, "E225", {"start": v(86.09, -8.18) * mm, "end": v(99.72, 39.37) * mm, "construction": true});
            skLineSegment(sketch, "E226", {"start": v(99.72, 39.37) * mm, "end": v(79.13, -6.87) * mm, "construction": true});
            skLineSegment(sketch, "E227", {"start": v(79.13, -6.87) * mm, "end": v(72.09, -4.85) * mm, "construction": true});
            skLineSegment(sketch, "E228", {"start": v(72.09, -4.85) * mm, "end": v(99.72, 39.37) * mm, "construction": true});
            skLineSegment(sketch, "E229", {"start": v(98.83, -5.07) * mm, "end": v(98.83, -8.58) * mm});
            skLineSegment(sketch, "E230", {"start": v(94.42, -4.76) * mm, "end": v(93.93, -8.24) * mm});
            skLineSegment(sketch, "E231", {"start": v(92.66, -4.51) * mm, "end": v(92.17, -8) * mm});
            skLineSegment(sketch, "E232", {"start": v(88.33, -3.6) * mm, "end": v(87.36, -6.97) * mm});
            skLineSegment(sketch, "E233", {"start": v(86.62, -3.1) * mm, "end": v(85.65, -6.48) * mm});
            skLineSegment(sketch, "E234", {"start": v(82.46, -1.6) * mm, "end": v(81.03, -4.8) * mm});
            skLineSegment(sketch, "E235", {"start": v(80.83, -0.87) * mm, "end": v(79.4, -4.07) * mm});
            skLineSegment(sketch, "E236", {"start": v(77.1, 3.18) * mm, "end": v(76.17, 1.67) * mm});
            skArc(sketch, "E237.trimOffspring", {"start": v(92.17, -8) * mm, "mid": v(93.05, -8.12) * mm, "end": v(93.93, -8.24) * mm});
            skArc(sketch, "E238.trimOffspring", {"start": v(98.83, -8.58) * mm, "mid": v(99.28, -8.59) * mm, "end": v(99.72, -8.59) * mm});
            skArc(sketch, "E239", {"start": v(85.65, -6.48) * mm, "mid": v(86.07, -6.6) * mm, "end": v(86.5, -6.73) * mm});
            skLineSegment(sketch, "E240", {"start": v(85.65, -6.48) * mm, "end": v(87.36, -6.97) * mm});
            skArc(sketch, "E241.MirrorCS", {"start": v(107.27, -8) * mm, "mid": v(106.4, -8.12) * mm, "end": v(105.51, -8.24) * mm});
            skArc(sketch, "E242.MirrorCS", {"start": v(120.04, -4.07) * mm, "mid": v(119.23, -4.44) * mm, "end": v(118.41, -4.8) * mm});
            skArc(sketch, "E243.MirrorCS", {"start": v(100.6, -8.58) * mm, "mid": v(100.16, -8.59) * mm, "end": v(99.72, -8.59) * mm});
            skArc(sketch, "E244.MirrorCS", {"start": v(113.8, -6.48) * mm, "mid": v(113.37, -6.6) * mm, "end": v(112.94, -6.73) * mm});
            skArc(sketch, "E245.MirrorCS", {"start": v(122.33, 3.18) * mm, "mid": v(111.48, -1.65) * mm, "end": v(99.72, -3.3) * mm});
            skArc(sketch, "E246.MirrorCS", {"start": v(123.28, 1.67) * mm, "mid": v(111.97, -3.36) * mm, "end": v(99.72, -5.08) * mm});
            skLineSegment(sketch, "E247.MirrorCS", {"start": v(112.82, -3.1) * mm, "end": v(113.8, -6.48) * mm});
            skLineSegment(sketch, "E248.MirrorCS", {"start": v(118.6, -0.87) * mm, "end": v(120.04, -4.07) * mm});
            skLineSegment(sketch, "E249.MirrorCS", {"start": v(113.8, -6.48) * mm, "end": v(112.08, -6.97) * mm});
            skLineSegment(sketch, "E250.MirrorCS", {"start": v(105.03, -4.76) * mm, "end": v(105.51, -8.24) * mm});
            skLineSegment(sketch, "E251.MirrorCS", {"start": v(111.12, -3.6) * mm, "end": v(112.08, -6.97) * mm});
            skLineSegment(sketch, "E252.MirrorCS", {"start": v(100.6, -5.07) * mm, "end": v(100.6, -8.58) * mm});
            skLineSegment(sketch, "E253.MirrorCS", {"start": v(122.33, 3.18) * mm, "end": v(123.28, 1.67) * mm});
            skLineSegment(sketch, "E254.MirrorCS", {"start": v(106.79, -4.51) * mm, "end": v(107.27, -8) * mm});
            skLineSegment(sketch, "E255.MirrorCS", {"start": v(116.98, -1.6) * mm, "end": v(118.41, -4.8) * mm});
            skLineSegment(sketch, "E256", {"start": v(69.57, 5.84) * mm, "end": v(141.67, 5.84) * mm, "construction": true});
            skLineSegment(sketch, "E257", {"start": v(71.27, 5.84) * mm, "end": v(75.99, 3.89) * mm});
            skLineSegment(sketch, "E258", {"start": v(75.99, 3.89) * mm, "end": v(75.99, 5) * mm});
            skLineSegment(sketch, "E259", {"start": v(75.99, 5) * mm, "end": v(120.89, 5) * mm});
            skLineSegment(sketch, "E260", {"start": v(120.89, 5) * mm, "end": v(122.08, 3.89) * mm});
            skLineSegment(sketch, "E261", {"start": v(122.08, 3.89) * mm, "end": v(127.54, 3.89) * mm});
            skLineSegment(sketch, "E262", {"start": v(127.54, 3.89) * mm, "end": v(126, 5.84) * mm});
            skLineSegment(sketch, "E263.MirrorCS", {"start": v(75.99, 6.68) * mm, "end": v(120.89, 6.68) * mm});
            skLineSegment(sketch, "E264.MirrorCS", {"start": v(71.27, 5.84) * mm, "end": v(75.99, 7.8) * mm});
            skLineSegment(sketch, "E265.MirrorCS", {"start": v(120.89, 6.68) * mm, "end": v(122.08, 7.8) * mm});
            skLineSegment(sketch, "E266.MirrorCS", {"start": v(75.99, 7.8) * mm, "end": v(75.99, 6.68) * mm});
            skLineSegment(sketch, "E267.MirrorCS", {"start": v(122.08, 7.8) * mm, "end": v(127.54, 7.8) * mm});
            skLineSegment(sketch, "E268.MirrorCS", {"start": v(127.54, 7.8) * mm, "end": v(126, 5.84) * mm});
            skSolve(sketch);
        }
        {
            var Q0;
            Q0 = qSketchRegion(id + "F14", true);
            extrude(context, id + "F15", {"entities" : qUnion([Q0]), "operationType" : NewBodyOperationType.ADD, "endBound" : BoundingType.UP_TO_NEXT, "oppositeDirection" : true, "depth" : 25.4 * mm, "offsetDistance" : 25.4 * mm});
        }
        {
            var Q0;
            Q0=qCreatedBy(id+"F12.planeOp",FACE);
            var sketch = newSketch(context, id + "F16", { "sketchPlane" : qUnion([Q0])});
            skLineSegment(sketch, "E269", {"start": v(0, 0) * mm, "end": v(0, 23.86) * mm, "construction": true});
            skPoint(sketch, "E270", {"position": v(0, 13.34) * mm});
            skCircle(sketch, "E271", {"center": v(0, 13.34) * mm, "radius": 8.26 * mm});
            skArc(sketch, "E272", {"start": v(8.72, 21.17) * mm, "mid": v(0.07, 25.06) * mm, "end": v(-8.63, 21.27) * mm});
            skLineSegment(sketch, "E273.bottom", {"start": v(-8.63, 31.17) * mm, "end": v(8.72, 31.17) * mm});
            skLineSegment(sketch, "E273.left", {"start": v(-8.63, 31.17) * mm, "end": v(-8.63, 21.27) * mm});
            skLineSegment(sketch, "E273.right", {"start": v(8.72, 31.17) * mm, "end": v(8.72, 21.17) * mm});
            skSolve(sketch);
        }
        {
            var Q0;
            Q0 = qSketchRegion(id + "F16", true);
            extrude(context, id + "F17", {"entities" : qUnion([Q0]), "operationType" : NewBodyOperationType.REMOVE, "oppositeDirection" : true, "depth" : 127 * mm, "offsetDistance" : 25.4 * mm});
        }
        {
            var Q0;
            Q0=qCreatedBy(makeId("Front.planeOp"),FACE);
            cPlane(context, id + "F18", {"entities" : qUnion([Q0]), "cplaneType" : CPlaneType.OFFSET, "offset" : 22.22 * mm, "width" : 152.4 * mm, "height" : 152.4 * mm});
        }
        {
            var Q0;
            Q0=qCreatedBy(id+"F18.planeOp",FACE);
            var sketch = newSketch(context, id + "F19", { "sketchPlane" : qUnion([Q0])});
            skLineSegment(sketch, "E274", {"start": v(45.26, 5.78) * mm, "end": v(45.26, -9.71) * mm, "construction": true});
            skLineSegment(sketch, "E275", {"start": v(42.88, 5.72) * mm, "end": v(42.88, -9.9) * mm, "construction": true});
            skLineSegment(sketch, "E276", {"start": v(154, 5.82) * mm, "end": v(154, -7.35) * mm, "construction": true});
            skLineSegment(sketch, "E277", {"start": v(156.39, 5.88) * mm, "end": v(156.39, -8) * mm, "construction": true});
            skLineSegment(sketch, "E278", {"start": v(30.8, 3.17) * mm, "end": v(170.82, 3.18) * mm, "construction": true});
            skPoint(sketch, "E279", {"position": v(44.07, 1.98) * mm});
            skPoint(sketch, "E280", {"position": v(155.2, 1.98) * mm});
            skArc(sketch, "E281", {"start": v(164, 3.18) * mm, "mid": v(155.2, 10.87) * mm, "end": v(146.38, 3.18) * mm});
            skLineSegment(sketch, "E282", {"start": v(146.38, 3.18) * mm, "end": v(164, 3.18) * mm});
            skArc(sketch, "E283", {"start": v(52.88, 3.17) * mm, "mid": v(44.07, 10.87) * mm, "end": v(35.26, 3.17) * mm});
            skLineSegment(sketch, "E284", {"start": v(35.26, 3.17) * mm, "end": v(52.88, 3.17) * mm});
            skSolve(sketch);
        }
        {
            var Q0;
            Q0 = qSketchRegion(id + "F19", true);
            extrude(context, id + "F20", {"entities" : qUnion([Q0]), "operationType" : NewBodyOperationType.ADD, "oppositeDirection" : true, "depth" : 2.54 * mm, "offsetDistance" : 25.4 * mm});
        }
        {
            var Q0;
            Q0=qCreatedBy(makeId("Front.planeOp"),FACE);
            cPlane(context, id + "F21", {"entities" : qUnion([Q0]), "cplaneType" : CPlaneType.OFFSET, "offset" : 22.22 * mm, "oppositeDirection" : true, "width" : 152.4 * mm, "height" : 152.4 * mm});
        }
        {
            var Q0;
            Q0=qCreatedBy(id+"F21.planeOp",FACE);
            var sketch = newSketch(context, id + "F22", { "sketchPlane" : qUnion([Q0])});
            skLineSegment(sketch, "E285", {"start": v(42.88, 6.62) * mm, "end": v(42.88, -10.5) * mm, "construction": true});
            skLineSegment(sketch, "E286", {"start": v(20.5, 3.17) * mm, "end": v(175.37, 3.18) * mm, "construction": true});
            skLineSegment(sketch, "E287", {"start": v(154, 7.5) * mm, "end": v(154, -8.75) * mm, "construction": true});
            skPoint(sketch, "E288", {"position": v(155.2, 1.98) * mm});
            skPoint(sketch, "E289", {"position": v(44.07, 1.98) * mm});
            skArc(sketch, "E290", {"start": v(52.88, 3.17) * mm, "mid": v(44.07, 10.87) * mm, "end": v(35.26, 3.17) * mm});
            skLineSegment(sketch, "E291", {"start": v(52.88, 3.17) * mm, "end": v(35.26, 3.17) * mm});
            skArc(sketch, "E292", {"start": v(164, 3.18) * mm, "mid": v(155.2, 10.87) * mm, "end": v(146.38, 3.18) * mm});
            skLineSegment(sketch, "E293", {"start": v(164, 3.18) * mm, "end": v(146.38, 3.18) * mm});
            skSolve(sketch);
        }
        {
            var Q0;
            Q0 = qSketchRegion(id + "F22", true);
            extrude(context, id + "F23", {"entities" : qUnion([Q0]), "operationType" : NewBodyOperationType.ADD, "depth" : 2.54 * mm, "offsetDistance" : 25.4 * mm});
        }
        {
            var Q0;
            Q0=makeQuery(id+"F1.opExtrude","CAP_EDGE",EDGE,{"disambiguationData":[OSD([sQuery(id+"F0.wireOp",EDGE,"E10")])],"isStart":false});
            var Q1;
            Q1=makeQuery(id+"F1.opExtrude","CAP_EDGE",EDGE,{"disambiguationData":[OSD([sQuery(id+"F0.wireOp",EDGE,"E10")])],"isStart":true});
            var Q2;
            Q2=makeQuery(id+"F1.opExtrude","CAP_EDGE",EDGE,{"disambiguationData":[OSD([sQuery(id+"F0.wireOp",EDGE,"E11")])],"isStart":false});
            var Q3;
            Q3=makeQuery(id+"F1.opExtrude","CAP_EDGE",EDGE,{"disambiguationData":[OSD([sQuery(id+"F0.wireOp",EDGE,"E11")])],"isStart":true});
            fillet(context, id + "F24", {"entities" : qUnion([Q0, Q1, Q2, Q3]), "radius" : 7.62 * mm, "tangentPropagation" : true, "allowEdgeOverflow" : false});
        }
        {
            var Q0;
            Q0=makeQuery(id+"F1.opExtrude","SWEPT_EDGE",EDGE,{"disambiguationData":[OSD([sQuery(id+"F0.wireOp",EDGE,"E9.0"),sQuery(id+"F0.wireOp",EDGE,"E11")])]});
            var Q1;
            Q1=makeQuery(id+"F24.opFillet","BLEND_EDGE",EDGE,{"blendedFrom":[makeQuery(id+"F1.opExtrude","CAP_EDGE",EDGE,{"disambiguationData":[OSD([sQuery(id+"F0.wireOp",EDGE,"E11")])],"isStart":false}),makeQuery(id+"F1.opExtrude","SWEPT_FACE",FACE,{"disambiguationData":[OSD([sQuery(id+"F0.wireOp",EDGE,"E9.0")])]})],"blendedInto":[makeQuery(id+"F1.opExtrude","SWEPT_FACE",FACE,{"disambiguationData":[OSD([sQuery(id+"F0.wireOp",EDGE,"E9.0")])]})]});
            var Q2;
            Q2=makeQuery(id+"F1.opExtrude","SWEPT_EDGE",EDGE,{"disambiguationData":[OSD([sQuery(id+"F0.wireOp",EDGE,"E8"),sQuery(id+"F0.wireOp",EDGE,"E11")])]});
            var Q3;
            Q3=makeQuery(id+"F1.opExtrude","CAP_EDGE",EDGE,{"disambiguationData":[OSD([sQuery(id+"F0.wireOp",EDGE,"E4")])],"isStart":false});
            var Q4;
            Q4=makeQuery(id+"F1.opExtrude","CAP_EDGE",EDGE,{"disambiguationData":[OSD([sQuery(id+"F0.wireOp",EDGE,"E0")])],"isStart":false});
            var Q5;
            Q5=makeQuery(id+"F1.opExtrude","CAP_EDGE",EDGE,{"disambiguationData":[OSD([sQuery(id+"F0.wireOp",EDGE,"E9.4")])],"isStart":true});
            var Q6;
            Q6=makeQuery(id+"F1.opExtrude","CAP_EDGE",EDGE,{"disambiguationData":[OSD([sQuery(id+"F0.wireOp",EDGE,"E4")])],"isStart":true});
            var Q7;
            Q7=makeQuery(id+"F1.opExtrude","CAP_EDGE",EDGE,{"disambiguationData":[OSD([sQuery(id+"F0.wireOp",EDGE,"E9.5")])],"isStart":true});
            var Q8;
            Q8=makeQuery(id+"F1.opExtrude","CAP_EDGE",EDGE,{"disambiguationData":[OSD([sQuery(id+"F0.wireOp",EDGE,"E9.4")])],"isStart":false});
            var Q9;
            Q9=makeQuery(id+"F20.opExtrude","CAP_EDGE",EDGE,{"disambiguationData":[OSD([sQuery(id+"F19.wireOp",EDGE,"E283")])],"isStart":false});
            var Q10;
            Q10=makeQuery(id+"F23.opExtrude","CAP_EDGE",EDGE,{"disambiguationData":[OSD([sQuery(id+"F22.wireOp",EDGE,"E290")])],"isStart":false});
            var Q11;
            Q11=makeQuery(id+"F23.opExtrude","CAP_EDGE",EDGE,{"disambiguationData":[OSD([sQuery(id+"F22.wireOp",EDGE,"E292")])],"isStart":false});
            var Q12;
            Q12=makeQuery(id+"F20.opExtrude","CAP_EDGE",EDGE,{"disambiguationData":[OSD([sQuery(id+"F19.wireOp",EDGE,"E281")])],"isStart":false});
            fillet(context, id + "F25", {"entities" : qUnion([Q0, Q1, Q2, Q3, Q4, Q5, Q6, Q7, Q8, Q9, Q10, Q11, Q12]), "radius" : 1.27 * mm, "tangentPropagation" : true, "allowEdgeOverflow" : false});
        }
    });